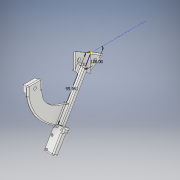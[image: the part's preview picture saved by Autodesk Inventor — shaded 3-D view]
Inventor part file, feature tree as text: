
AUTODESK INVENTOR PART (.ipt)
format: ipt  version: 2019.4 (Build 234330000, 330)  size: 962,560 bytes
history: native  units: mm
features: fillet x24, sketch x15, extrude x14, pattern_circular x3
ambient origin geometry x8: Origin, YZ Plane, XZ Plane, XY Plane, X Axis, Y Axis, Z Axis, Center Point
bodies: Body1 (feature_tree)
feature tree (56):
  extrude  "Extrusion5"  TaperAngle=120.0deg  [1 undecoded]
  extrude  "Extrusion6"  Depth=5.0mm TaperAngle=0.0deg
  extrude  "Extrusion7"  TaperAngle=60.0deg  [1 undecoded]
  sketch  "Sketch8"  dims[d31=20.0mm d32=60.0deg]
  extrude  "Extrusion10"  TaperAngle=60.0deg  [1 undecoded]
  extrude  "Extrusion11"  Depth=5.5mm
  extrude  "Extrusion12"  Depth=5.5mm
  sketch  "Sketch14"  dims[d40=5.0mm d41=0.0mm d42=95.981mm]
  extrude  "Extrusion13"  Depth=3.0mm
  extrude  "Extrusion14"  Depth=95.981mm
  pattern_circular  "Circular Pattern3"  Count=9  [1 undecoded]
  fillet  "Fillet2"  Radius=15.0mm
  fillet  "Fillet3"  Radius=30.0mm
  fillet  "Fillet4"  Radius=10.0mm
  fillet  "Fillet5"  Radius=2.5mm
  fillet  "Fillet6"  Radius=3.0mm
  fillet  "Fillet7"  Radius=3.5mm
  fillet  "Fillet8"  Radius=19.175mm
  fillet  "Fillet9"  Radius=2.5mm
  fillet  "Fillet10"  Radius=33.679mm
  fillet  "Fillet11"  Radius=10.775mm
  extrude  "Extrusion16"  TaperAngle=180.0deg  [1 undecoded]
  fillet  "Fillet17"  Radius=7.0mm
  fillet  "Fillet18"  Radius=3.5mm
  fillet  "Fillet19"  Radius=10.0mm
  fillet  "Fillet20"  Radius=3.5mm
  fillet  "Fillet21"  Radius=10.0mm
  pattern_circular  "Circular Pattern4"  Count=3 Angle=360.0deg
  fillet  "Fillet22"  Radius=2.0mm
  fillet  "Fillet23"  Radius=2.0mm
  fillet  "Fillet24"  Radius=2.0mm
  fillet  "Fillet25"  Radius=2.0mm
  fillet  "Fillet26"  Radius=2.0mm
  fillet  "Fillet27"  Radius=2.0mm
  extrude  "Extrusion17"  Depth=2.0mm
  pattern_circular  "Circular Pattern5"  [2 undecoded]
  extrude  "Extrusion18"  Depth=2.0mm
  extrude  "Extrusion19"  Depth=2.0mm
  extrude  "Extrusion20"  Depth=100.0mm
  extrude  "Extrusion21"  TaperAngle=180.0deg  [1 undecoded]
  fillet  "Fillet28"  Radius=5.0mm
  fillet  "Fillet29"  Radius=10.0mm
  fillet  "Fillet30"  Radius=15.0mm
  sketch  "Sketch5"  dims[d24=60.0mm d25=120.0deg]
  sketch  "Sketch6"  dims[d26=120.0deg d27=5.0mm d28=0.0mm]
  sketch  "Sketch7"  dims[d29=20.0mm d30=60.0deg]
  sketch  "Sketch11"  dims[d33=20.0mm d34=5.5mm]
  sketch  "Sketch12"  dims[d35=5.5mm d36=5.5mm]
  sketch  "Sketch13"  dims[d37=5.0mm d38=0.0mm d39=3.0mm]
  sketch  "Sketch15"  dims[d43=120.0deg]
  sketch  "Sketch16"  dims[d54=6.0mm]
  sketch  "Sketch17"  dims[d55=10.0mm]
  sketch  "Sketch18"  dims[d56=5.0mm]
  sketch  "Sketch19"  dims[d57=45.0deg]
  sketch  "Sketch20"  dims[d58=10.0mm d59=0.0mm]
  sketch  "Sketch21"  dims[d60=5.0mm d61=90.0mm d62=0.0mm d63=15.0mm d64=30.0mm d65=10.0mm d66=0.0mm d67=2.5mm d68=3.0mm d69=3.5mm d70=19.175mm d71=2.5mm d72=33.679mm d73=10.775mm d74=180.0deg d75=7.0mm d76=3.5mm d77=10.0mm d78=0.0mm d79=3.5mm d80=10.0mm d81=0.0mm d82=30.0mm d83=360.0deg d85=2.0mm d86=2.0mm d87=2.0mm d88=2.0mm d89=2.0mm d90=2.0mm d91=2.0mm d92=2.0mm d93=2.0mm d94=2.0mm d95=100.0mm d96=180.0deg d97=5.0mm d98=10.0mm d99=15.0mm d107=80.0mm d108=120.0deg d109=5.0mm d110=0.0mm d111=5.0mm d112=2.0mm d113=2.0mm d114=2.0mm d115=2.0mm d116=30.0mm d117=360.0deg d119=5.0mm d120=5.0mm d121=5.0mm d122=2.0mm d123=2.0mm d124=2.0mm d125=20.0mm d126=60.0deg d127=5.0mm d128=0.0mm d129=30.0mm d130=360.0deg d132=200.0mm d133=200.0mm d134=6.457718mm d135=24.43461mm d136=50.0mm d137=0.0mm d138=2.6mm d139=0.0mm d140=28.509mm d141=150.0deg d142=20.0mm d143=120.0deg d144=5.5mm d145=2.5mm d146=0.0mm d147=3.0mm d148=20.0mm d149=0.0mm d150=2.0mm d151=2.0mm d152=2.0mm]
note: 8 required parameter values undecoded (feature->parameter linkage not recoverable at this tier; creation-order binding heuristic only, values carry confidence <= 0.55)
